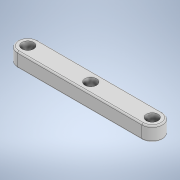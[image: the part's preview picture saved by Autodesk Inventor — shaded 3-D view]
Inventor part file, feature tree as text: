
AUTODESK INVENTOR PART (.ipt)
format: ipt  version: 2021 (Build 250183000, 183)  size: 126,464 bytes
history: native  units: mm
features: extrude x1, fillet x1, sketch x1
ambient origin geometry x8: Origin, YZ Plane, XZ Plane, XY Plane, X Axis, Y Axis, Z Axis, Center Point
bodies: Solid1 (feature_tree)
feature tree (3):
  extrude  "Extrusion1"  Depth=4.66mm
  fillet  "Fillet1"  Radius=2.66mm
  sketch  "Sketch1"  dims[d0=28.33mm d1=4.66mm d2=2.66mm d3=14.0mm d4=3.33mm d5=0.0mm d6=0.33mm]
